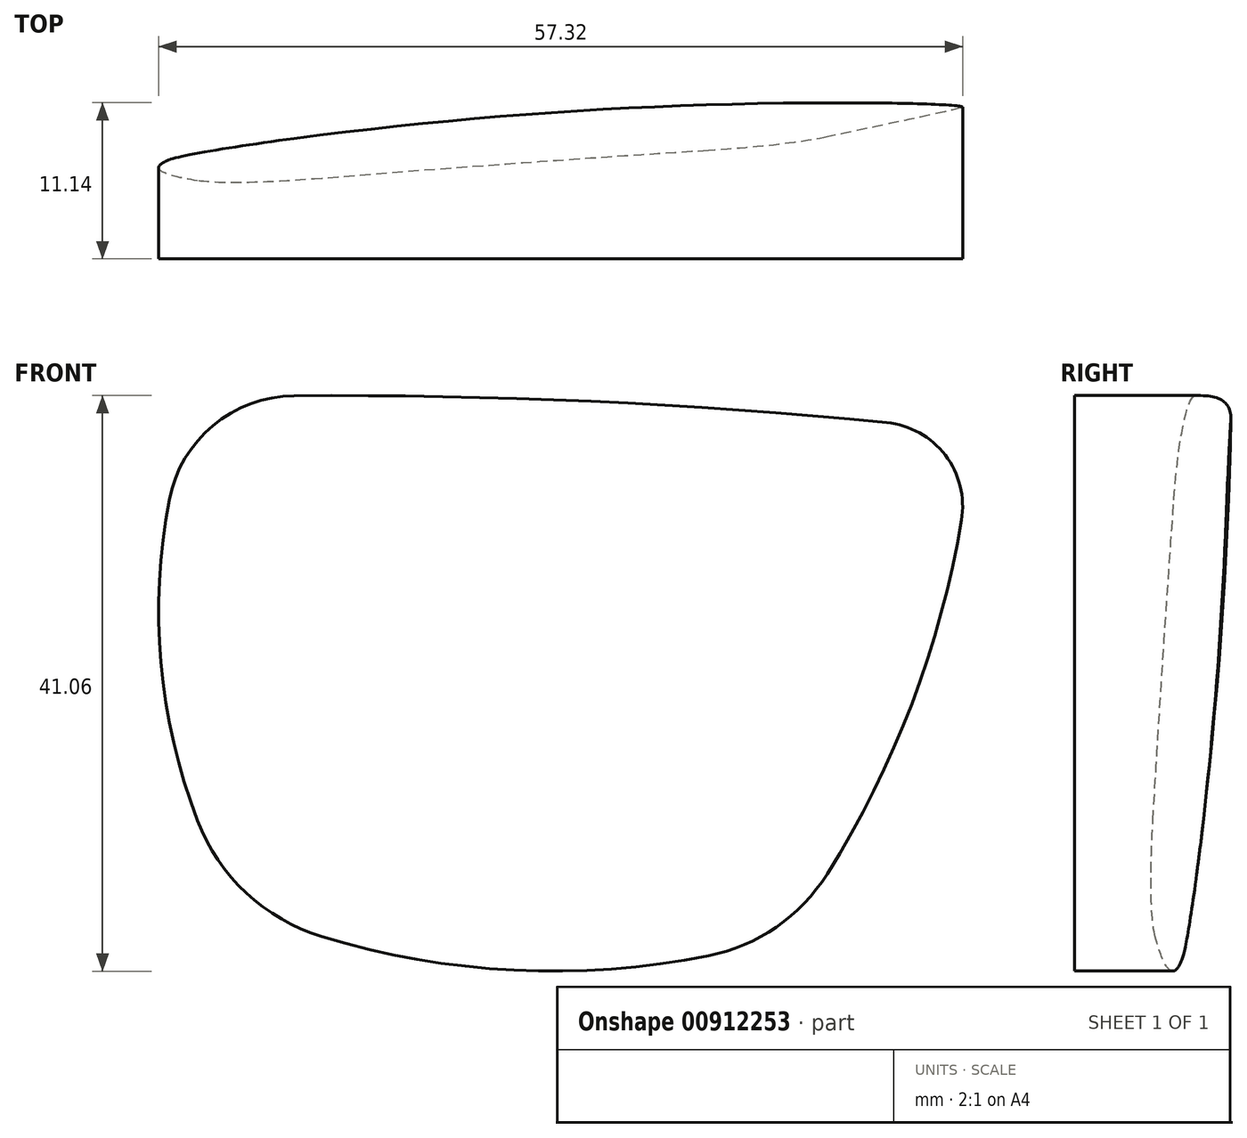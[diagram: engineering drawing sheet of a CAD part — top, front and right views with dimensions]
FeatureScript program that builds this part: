
annotation { "Feature Type Name" : "Feature", "Feature Type Description" : "" }
export const myFeature = defineFeature(function(context is Context, id is Id, definition is map)
    precondition{}
    {
        {
            var Q0;
            Q0=qCreatedBy(makeId("Front.planeOp"),FACE);
            var sketch = newSketch(context, id + "F0", { "sketchPlane" : qUnion([Q0])});
            skArc(sketch, "E0.0.0", {"start": v(-34.1, 10.7) * mm, "mid": v(-34.33, -2) * mm, "end": v(-31.21, -14.33) * mm, "construction": true});
            skArc(sketch, "E0.0.1", {"start": v(-31.21, -14.33) * mm, "mid": v(-26.88, -20.6) * mm, "end": v(-20.26, -24.39) * mm, "construction": true});
            skArc(sketch, "E0.0.2", {"start": v(-20.26, -24.39) * mm, "mid": v(-5.74, -26.92) * mm, "end": v(8.96, -25.84) * mm, "construction": true});
            skArc(sketch, "E0.0.3", {"start": v(8.96, -25.84) * mm, "mid": v(15.05, -23.27) * mm, "end": v(19.63, -18.5) * mm, "construction": true});
            skArc(sketch, "E0.0.4", {"start": v(19.63, -18.5) * mm, "mid": v(26.11, -5.85) * mm, "end": v(30.26, 7.75) * mm, "construction": true});
            skLineSegment(sketch, "E0.0.5", {"start": v(30.26, 7.75) * mm, "end": v(34.76, 7.75) * mm, "construction": true});
            skLineSegment(sketch, "E0.0.6", {"start": v(34.76, 7.75) * mm, "end": v(34.76, 21.75) * mm, "construction": true});
            skLineSegment(sketch, "E0.0.7", {"start": v(34.76, 21.75) * mm, "end": v(-21.24, 21.75) * mm, "construction": true});
            skArc(sketch, "E0.0.8", {"start": v(-21.24, 21.75) * mm, "mid": v(-29.71, 18.6) * mm, "end": v(-34.1, 10.7) * mm, "construction": true});
            skPoint(sketch, "E1.visualSharp", {"position": v(28.45, 17.95) * mm});
            skArc(sketch, "E2", {"start": v(21.01, 15.53) * mm, "mid": v(-0.09, 17.05) * mm, "end": v(-21.24, 17.45) * mm});
            skLineSegment(sketch, "E3", {"start": v(-21.24, 24.56) * mm, "end": v(-21.24, 13.97) * mm, "construction": true});
            skArc(sketch, "E4.filletArc", {"start": v(26.34, 8.57) * mm, "mid": v(25.19, 13.2) * mm, "end": v(21.01, 15.53) * mm});
            skArc(sketch, "E5.0", {"start": v(8.3, -22.5) * mm, "mid": v(13.14, -20.46) * mm, "end": v(16.77, -16.66) * mm});
            skArc(sketch, "E5.2", {"start": v(-28.13, -12.86) * mm, "mid": v(-24.66, -18.02) * mm, "end": v(-19.27, -21.14) * mm});
            skArc(sketch, "E6", {"start": v(16.77, -16.66) * mm, "mid": v(22.8, -4.52) * mm, "end": v(26.34, 8.57) * mm});
            skArc(sketch, "E7", {"start": v(-30.15, 10.02) * mm, "mid": v(-30.74, -1.56) * mm, "end": v(-28.13, -12.86) * mm});
            skArc(sketch, "E8.0", {"start": v(-19.27, -21.14) * mm, "mid": v(-5.57, -23.53) * mm, "end": v(8.3, -22.5) * mm});
            skArc(sketch, "E9", {"start": v(-21.24, 17.45) * mm, "mid": v(-27.03, 15.33) * mm, "end": v(-30.15, 10.02) * mm});
            skSolve(sketch);
        }
        {
            var Q0;
            Q0=makeQuery(id+"F0.imprint","IMPRINT",FACE,{"disambiguationData":[TD([[makeQuery(id+"F0.imprint","IMPRINT",EDGE,{"derivedFrom":sQuery(id+"F0.wireOp",EDGE,"E2")}),1.0]])]});
            extrude(context, id + "F1", {"entities" : qUnion([Q0]), "oppositeDirection" : true, "depth" : 25 * mm});
        }
        {
            var Q0;
            Q0=qCreatedBy(makeId("Top.planeOp"),FACE);
            cPlane(context, id + "F2", {"entities" : qUnion([Q0]), "cplaneType" : CPlaneType.OFFSET, "offset" : 22 * mm, "width" : 150 * mm, "height" : 150 * mm});
        }
        {
            var Q0;
            Q0=qCreatedBy(id+"F2.planeOp",FACE);
            var sketch = newSketch(context, id + "F3", { "sketchPlane" : qUnion([Q0])});
            skArc(sketch, "E10", {"start": v(318, -293) * mm, "mid": v(18, 7) * mm, "end": v(-282, -293) * mm});
            skLineSegment(sketch, "E11", {"start": v(-372.73, -293) * mm, "end": v(417.57, -293) * mm, "construction": true});
            skLineSegment(sketch, "E12", {"start": v(-282, -293) * mm, "end": v(318, -293) * mm});
            skSolve(sketch);
        }
        {
            var Q0;
            Q0=makeQuery(id+"F3.imprint","IMPRINT",FACE,{"disambiguationData":[TD([[makeQuery(id+"F3.imprint","IMPRINT",EDGE,{"derivedFrom":sQuery(id+"F3.wireOp",EDGE,"E10")}),1.0]])]});
            var Q1;
            Q1=sQuery(id+"F3.wireOp",EDGE,"E12");
            revolve(context, id + "F4", {"entities" : qUnion([Q0]), "axis" : qUnion([Q1]), "revolveType" : RevolveType.SYMMETRIC, "angle" : 30 * degree});
        }
        {
            var Q0;
            Q0=makeQuery(id+"F1.opExtrude","SWEPT_BODY",BODY,{"disambiguationData":[OSD([sQuery(id+"F0.wireOp",EDGE,"E2"),sQuery(id+"F0.wireOp",EDGE,"E4.filletArc"),sQuery(id+"F0.wireOp",EDGE,"E5.0"),sQuery(id+"F0.wireOp",EDGE,"E5.2"),sQuery(id+"F0.wireOp",EDGE,"E6"),sQuery(id+"F0.wireOp",EDGE,"E7"),sQuery(id+"F0.wireOp",EDGE,"E8.0"),sQuery(id+"F0.wireOp",EDGE,"E9")])]});
            var Q1;
            Q1=makeQuery(id+"F4.opRevolve","SWEPT_BODY",BODY,{"disambiguationData":[OSD([sQuery(id+"F3.wireOp",EDGE,"E10"),sQuery(id+"F3.wireOp",EDGE,"E12")])]});
            booleanBodies(context, id + "F5", {"operationType" : BooleanOperationType.INTERSECTION, "tools" : qUnion([Q0, Q1])});
        }
        {
            var Q0;
            Q0=makeQuery(id+"F1.opExtrude","CAP_FACE",FACE,{"disambiguationData":[OSD([sQuery(id+"F0.wireOp",EDGE,"E2"),sQuery(id+"F0.wireOp",EDGE,"E4.filletArc"),sQuery(id+"F0.wireOp",EDGE,"E5.0"),sQuery(id+"F0.wireOp",EDGE,"E5.2"),sQuery(id+"F0.wireOp",EDGE,"E6"),sQuery(id+"F0.wireOp",EDGE,"E7"),sQuery(id+"F0.wireOp",EDGE,"E8.0"),sQuery(id+"F0.wireOp",EDGE,"E9")])],"isStart":true});
            extrude(context, id + "F6", {"entities" : qUnion([Q0]), "operationType" : NewBodyOperationType.ADD, "depth" : 4.2 * mm, "offsetDistance" : 25 * mm});
        }
    });
